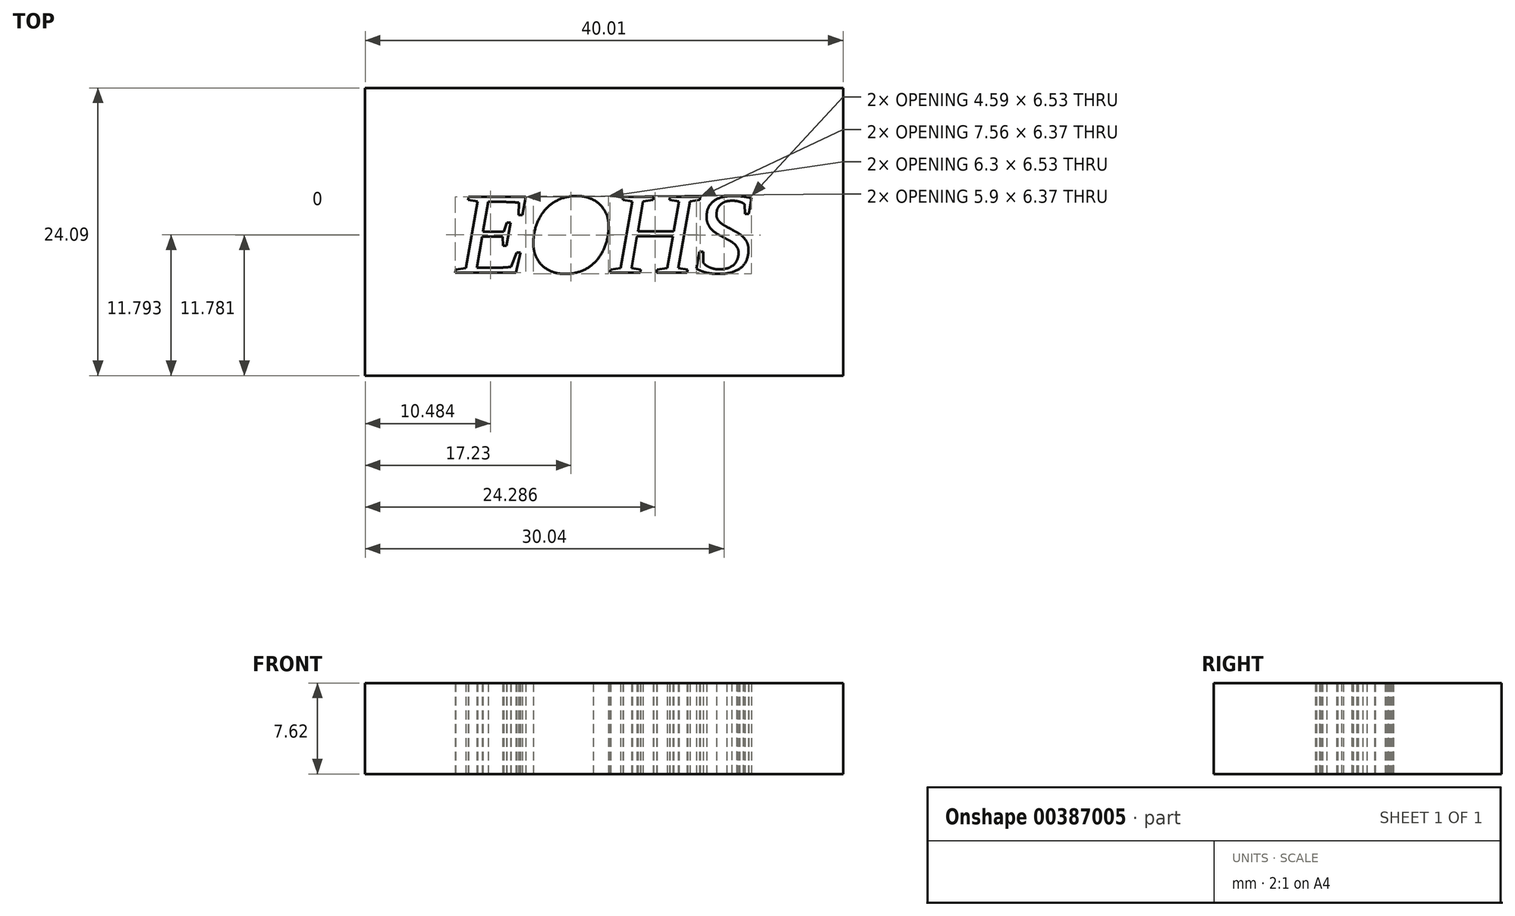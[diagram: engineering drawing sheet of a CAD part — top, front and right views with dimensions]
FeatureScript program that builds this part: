
annotation { "Feature Type Name" : "Feature", "Feature Type Description" : "" }
export const myFeature = defineFeature(function(context is Context, id is Id, definition is map)
    precondition{}
    {
        {
            var Q0;
            Q0=qCreatedBy(makeId("Top.planeOp"),FACE);
            var sketch = newSketch(context, id + "F0", { "sketchPlane" : qUnion([Q0])});
            skText(sketch, "E0", { "text": "EOHS", "fontName": "Tinos-Italic.ttf"});
            skLineSegment(sketch, "E1.bottom", {"start": v(-20.17, 15.9) * mm, "end": v(19.84, 15.9) * mm});
            skLineSegment(sketch, "E1.top", {"start": v(-20.17, -8.2) * mm, "end": v(19.84, -8.2) * mm});
            skLineSegment(sketch, "E1.left", {"start": v(-20.17, 15.9) * mm, "end": v(-20.17, -8.2) * mm});
            skLineSegment(sketch, "E1.right", {"start": v(19.84, 15.9) * mm, "end": v(19.84, -8.2) * mm});
            const initialGuessF0  = {"E0": [-0.01252, 0.00041, 1, 0, 0.007]};
            skSetInitialGuess(sketch, initialGuessF0);
            skSolve(sketch);
        }
        {
            var Q0;
            Q0=makeQuery(id+"F0.imprint","IMPRINT",FACE,{"disambiguationData":[TD([[makeQuery(id+"F0.imprint","IMPRINT",EDGE,{"derivedFrom":sQuery(id+"F0.wireOp",EDGE,"E0.sketch_text.stroke-0")}),1.0]])]});
            extrude(context, id + "F1", {"entities" : qUnion([Q0]), "depth" : 7.62 * mm});
        }
    });
